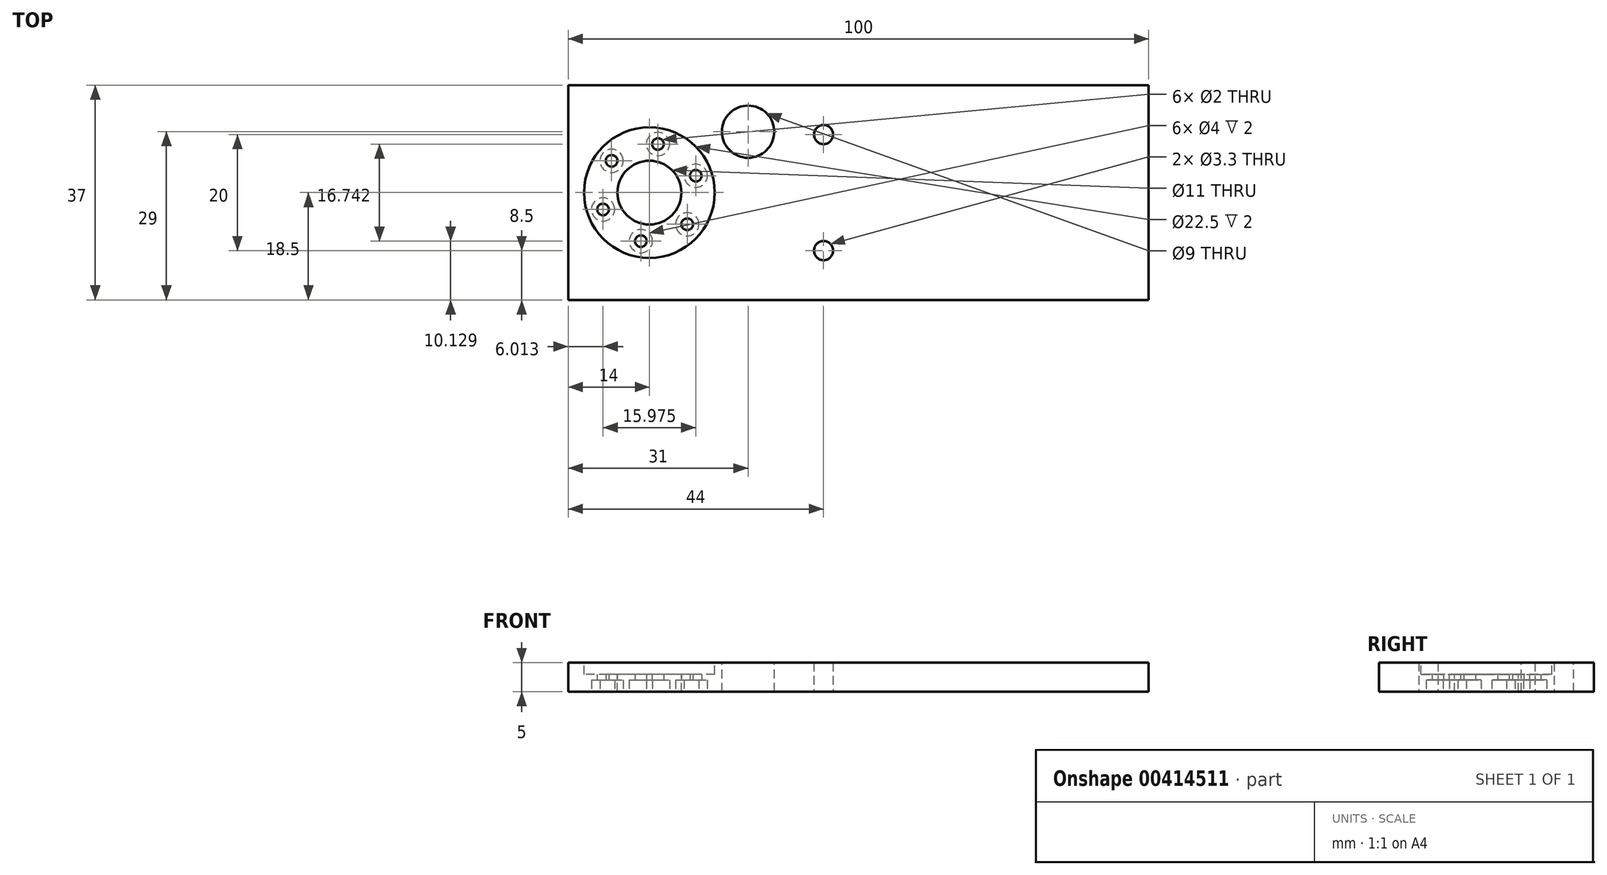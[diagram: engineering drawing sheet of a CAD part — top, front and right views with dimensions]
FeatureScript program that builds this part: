
annotation { "Feature Type Name" : "Feature", "Feature Type Description" : "" }
export const myFeature = defineFeature(function(context is Context, id is Id, definition is map)
    precondition{}
    {
        {
            var Q0;
            Q0=qCreatedBy(makeId("Top.planeOp"),FACE);
            var sketch = newSketch(context, id + "F0", { "sketchPlane" : qUnion([Q0])});
            skLineSegment(sketch, "E0.bottom", {"start": v(-50, 18.5) * mm, "end": v(50, 18.5) * mm});
            skLineSegment(sketch, "E0.top", {"start": v(-50, -18.5) * mm, "end": v(50, -18.5) * mm});
            skLineSegment(sketch, "E0.left", {"start": v(-50, 18.5) * mm, "end": v(-50, -18.5) * mm});
            skLineSegment(sketch, "E0.right", {"start": v(50, 18.5) * mm, "end": v(50, -18.5) * mm});
            skPoint(sketch, "E0.middle", {"position": v(0, 0) * mm});
            skSolve(sketch);
        }
        {
            var Q0;
            Q0 = qSketchRegion(id + "F0", true);
            extrude(context, id + "F1", {"entities" : qUnion([Q0]), "depth" : 5 * mm});
        }
        {
            var Q0;
            Q0=makeQuery(id+"F1.opExtrude","CAP_FACE",FACE,{"disambiguationData":[OSD([sQuery(id+"F0.wireOp",EDGE,"E0.bottom"),sQuery(id+"F0.wireOp",EDGE,"E0.top"),sQuery(id+"F0.wireOp",EDGE,"E0.left"),sQuery(id+"F0.wireOp",EDGE,"E0.right")])],"isStart":false});
            var sketch = newSketch(context, id + "F2", { "sketchPlane" : qUnion([Q0])});
            skCircle(sketch, "E1", {"center": v(-36, 0) * mm, "radius": 5.5 * mm});
            skSolve(sketch);
        }
        {
            var Q0;
            Q0 = qSketchRegion(id + "F2", true);
            extrude(context, id + "F3", {"entities" : qUnion([Q0]), "operationType" : NewBodyOperationType.REMOVE, "oppositeDirection" : true, "depth" : 5 * mm});
        }
        {
            var Q0;
            Q0=makeQuery(id+"F1.opExtrude","CAP_FACE",FACE,{"disambiguationData":[OSD([sQuery(id+"F0.wireOp",EDGE,"E0.bottom"),sQuery(id+"F0.wireOp",EDGE,"E0.top"),sQuery(id+"F0.wireOp",EDGE,"E0.left"),sQuery(id+"F0.wireOp",EDGE,"E0.right")])],"isStart":false});
            var sketch = newSketch(context, id + "F4", { "sketchPlane" : qUnion([Q0])});
            skCircle(sketch, "E2", {"center": v(-36, 0) * mm, "radius": 11.25 * mm});
            skSolve(sketch);
        }
        {
            var Q0;
            Q0 = qSketchRegion(id + "F4", true);
            extrude(context, id + "F5", {"entities" : qUnion([Q0]), "operationType" : NewBodyOperationType.REMOVE, "oppositeDirection" : true, "depth" : 2 * mm});
        }
        {
            var Q0;
            Q0=makeQuery(id+"F1.opExtrude","CAP_FACE",FACE,{"disambiguationData":[OSD([sQuery(id+"F0.wireOp",EDGE,"E0.bottom"),sQuery(id+"F0.wireOp",EDGE,"E0.top"),sQuery(id+"F0.wireOp",EDGE,"E0.left"),sQuery(id+"F0.wireOp",EDGE,"E0.right")])],"isStart":true});
            var sketch = newSketch(context, id + "F6", { "sketchPlane" : qUnion([Q0])});
            skCircle(sketch, "E3.cCircle", {"center": v(-36, 0) * mm, "radius": 8.5 * mm, "construction": true});
            skLineSegment(sketch, "E3.0", {"start": v(-37.48, 8.37) * mm, "end": v(-29.49, 5.46) * mm, "construction": true});
            skLineSegment(sketch, "E3.1", {"start": v(-29.49, 5.46) * mm, "end": v(-28.01, -2.9) * mm, "construction": true});
            skLineSegment(sketch, "E3.2", {"start": v(-28.01, -2.9) * mm, "end": v(-34.52, -8.37) * mm, "construction": true});
            skLineSegment(sketch, "E3.3", {"start": v(-34.52, -8.37) * mm, "end": v(-42.51, -5.46) * mm, "construction": true});
            skLineSegment(sketch, "E3.4", {"start": v(-42.51, -5.46) * mm, "end": v(-43.99, 2.9) * mm, "construction": true});
            skLineSegment(sketch, "E3.5", {"start": v(-43.99, 2.9) * mm, "end": v(-37.48, 8.37) * mm, "construction": true});
            skLineSegment(sketch, "E4", {"start": v(-37.48, 8.37) * mm, "end": v(-36, 0) * mm, "construction": true});
            skLineSegment(sketch, "E5", {"start": v(-36, 18.5) * mm, "end": v(-36, 0) * mm, "construction": true});
            skPoint(sketch, "E6", {"position": v(-37.48, 8.37) * mm});
            skPoint(sketch, "E7", {"position": v(-43.99, 2.9) * mm});
            skPoint(sketch, "E8", {"position": v(-42.51, -5.46) * mm});
            skPoint(sketch, "E9", {"position": v(-34.52, -8.37) * mm});
            skPoint(sketch, "E10", {"position": v(-28.01, -2.9) * mm});
            skPoint(sketch, "E11", {"position": v(-29.49, 5.46) * mm});
            skSolve(sketch);
        }
        {
            var Q0;
            Q0=sQuery(id+"F6.wireOp",VERTEX,"E6");
            var Q1;
            Q1=sQuery(id+"F6.wireOp",VERTEX,"E7");
            var Q2;
            Q2=sQuery(id+"F6.wireOp",VERTEX,"E8");
            var Q3;
            Q3=sQuery(id+"F6.wireOp",VERTEX,"E9");
            var Q4;
            Q4=sQuery(id+"F6.wireOp",VERTEX,"E10");
            var Q5;
            Q5=sQuery(id+"F6.wireOp",VERTEX,"E11");
            var Q6;
            Q6=makeQuery(id+"F1.opExtrude","SWEPT_BODY",BODY,{"disambiguationData":[OSD([sQuery(id+"F0.wireOp",EDGE,"E0.bottom"),sQuery(id+"F0.wireOp",EDGE,"E0.top"),sQuery(id+"F0.wireOp",EDGE,"E0.left"),sQuery(id+"F0.wireOp",EDGE,"E0.right")])]});
            hole(context, id + "F7", {"style" : HoleStyle.C_BORE, "endStyle" : HoleEndStyle.BLIND, "holeDiameter" : 2 * mm, "cBoreDiameter" : 4 * mm, "cBoreDepth" : 2 * mm, "holeDepth" : 6 * mm, "tappedDepth" : 5 * mm, "tapClearance" : 2, "startFromSketch" : true, "locations" : qUnion([Q0, Q1, Q2, Q3, Q4, Q5]), "scope" : qUnion([Q6])});
        }
        {
            var Q0;
            Q0=makeQuery(id+"F1.opExtrude","CAP_FACE",FACE,{"disambiguationData":[OSD([sQuery(id+"F0.wireOp",EDGE,"E0.bottom"),sQuery(id+"F0.wireOp",EDGE,"E0.top"),sQuery(id+"F0.wireOp",EDGE,"E0.left"),sQuery(id+"F0.wireOp",EDGE,"E0.right")])],"isStart":false});
            var sketch = newSketch(context, id + "F8", { "sketchPlane" : qUnion([Q0])});
            skPoint(sketch, "E12", {"position": v(-19, 10.5) * mm});
            skSolve(sketch);
        }
        {
            var Q0;
            Q0=sQuery(id+"F8.wireOp",VERTEX,"E12");
            var Q1;
            Q1=makeQuery(id+"F1.opExtrude","SWEPT_BODY",BODY,{"disambiguationData":[OSD([sQuery(id+"F0.wireOp",EDGE,"E0.bottom"),sQuery(id+"F0.wireOp",EDGE,"E0.top"),sQuery(id+"F0.wireOp",EDGE,"E0.left"),sQuery(id+"F0.wireOp",EDGE,"E0.right")])]});
            hole(context, id + "F9", {"style" : HoleStyle.SIMPLE, "endStyle" : HoleEndStyle.BLIND, "standardTappedOrClearance" : lookupTablePath({ "standard" : "ISO", "engagement" : "75%", "pitch" : "1 mm", "size" : "M10", "type" : "Tapped" }), "standardBlindInLast" : lookupTablePath({ "standard" : "ISO", "engagement" : "75%", "pitch" : "1 mm", "size" : "M10", "type" : "Tapped" }), "holeDiameter" : 9 * mm, "showTappedDepth" : true, "holeDepth" : 7 * mm, "tappedDepth" : 5 * mm, "tapClearance" : 2, "startFromSketch" : true, "locations" : qUnion([Q0]), "scope" : qUnion([Q1]), "majorDiameter" : 10 * mm});
        }
        {
            var Q0;
            Q0=makeQuery(id+"F1.opExtrude","CAP_FACE",FACE,{"disambiguationData":[OSD([sQuery(id+"F0.wireOp",EDGE,"E0.bottom"),sQuery(id+"F0.wireOp",EDGE,"E0.top"),sQuery(id+"F0.wireOp",EDGE,"E0.left"),sQuery(id+"F0.wireOp",EDGE,"E0.right")])],"isStart":true});
            var sketch = newSketch(context, id + "F10", { "sketchPlane" : qUnion([Q0])});
            skLineSegment(sketch, "E13", {"start": v(-6, 10) * mm, "end": v(-6, -10) * mm, "construction": true});
            skPoint(sketch, "E14", {"position": v(-6, 10) * mm});
            skPoint(sketch, "E15", {"position": v(-6, -10) * mm});
            skSolve(sketch);
        }
        {
            var Q0;
            Q0=sQuery(id+"F10.wireOp",VERTEX,"E14");
            var Q1;
            Q1=sQuery(id+"F10.wireOp",VERTEX,"E15");
            var Q2;
            Q2=makeQuery(id+"F1.opExtrude","SWEPT_BODY",BODY,{"disambiguationData":[OSD([sQuery(id+"F0.wireOp",EDGE,"E0.bottom"),sQuery(id+"F0.wireOp",EDGE,"E0.top"),sQuery(id+"F0.wireOp",EDGE,"E0.left"),sQuery(id+"F0.wireOp",EDGE,"E0.right")])]});
            hole(context, id + "F11", {"style" : HoleStyle.SIMPLE, "endStyle" : HoleEndStyle.BLIND, "standardTappedOrClearance" : lookupTablePath({ "standard" : "ISO", "fit" : "Normal", "size" : "M3", "type" : "Clearance" }), "standardBlindInLast" : lookupTablePath({ "fit" : "Standard", "standard" : "ISO", "size" : "M3", "type" : "Clearance" }), "holeDiameter" : 3.3 * mm, "holeDepth" : 6 * mm, "tappedDepth" : 5 * mm, "tapClearance" : 2, "startFromSketch" : true, "locations" : qUnion([Q0, Q1]), "scope" : qUnion([Q2])});
        }
    });
